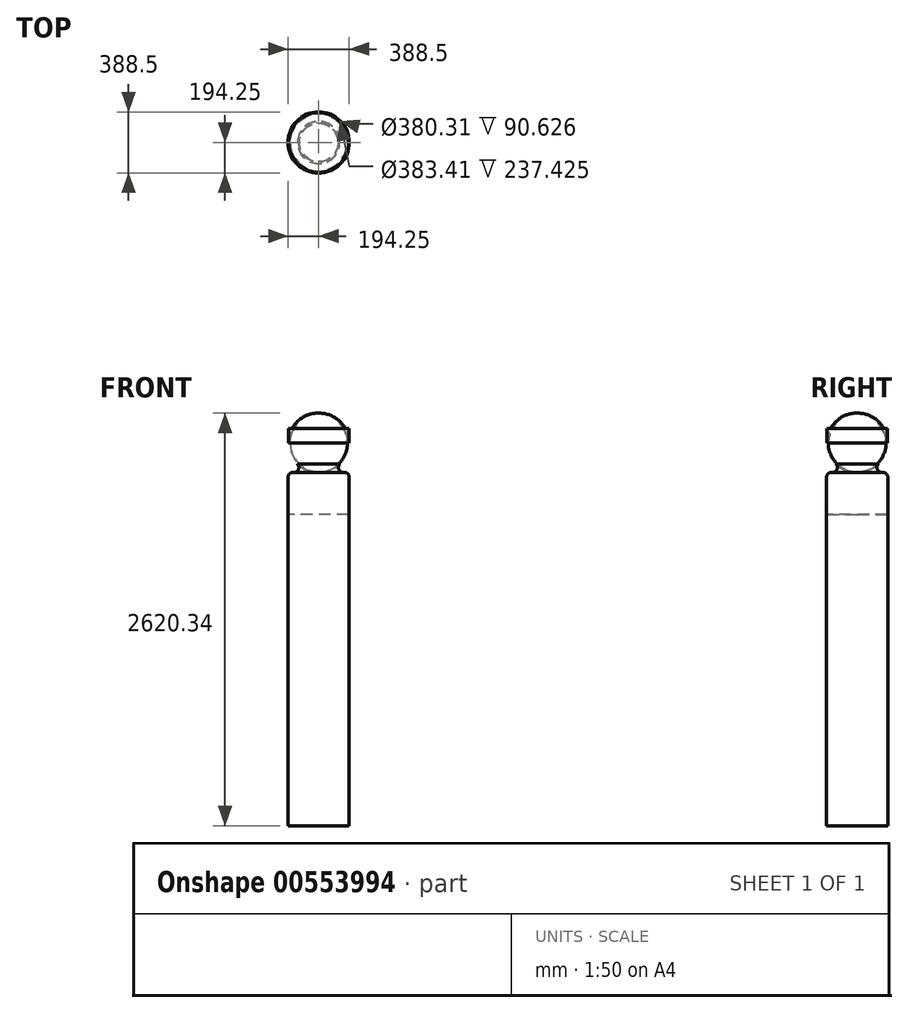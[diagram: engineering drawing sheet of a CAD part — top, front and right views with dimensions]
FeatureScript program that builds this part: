
annotation { "Feature Type Name" : "Feature", "Feature Type Description" : "" }
export const myFeature = defineFeature(function(context is Context, id is Id, definition is map)
    precondition{}
    {
        {
            var Q0;
            Q0=qCreatedBy(makeId("Top.planeOp"),FACE);
            var sketch = newSketch(context, id + "F0", { "sketchPlane" : qUnion([Q0])});
            skCircle(sketch, "E0", {"center": v(0, 0) * mm, "radius": 192.7 * mm});
            skSolve(sketch);
        }
        {
            var Q0;
            Q0=makeQuery(id+"F0.imprint","IMPRINT",FACE,{"disambiguationData":[TD([[makeQuery(id+"F0.imprint","IMPRINT",EDGE,{"derivedFrom":sQuery(id+"F0.wireOp",EDGE,"E0")}),1.0]])]});
            extrude(context, id + "F1", {"entities" : qUnion([Q0]), "depth" : 278.82 * mm, "offsetDistance" : 25.4 * mm});
        }
        {
            var Q0;
            Q0=makeQuery(id+"F1.opExtrude","CAP_FACE",FACE,{"disambiguationData":[OSD([sQuery(id+"F0.wireOp",EDGE,"E0")])],"isStart":true});
            fillet(context, id + "F2", {"entities" : qUnion([Q0]), "radius" : 188.2 * mm, "tangentPropagation" : true, "allowEdgeOverflow" : false});
        }
        {
            var Q0;
            Q0=qCreatedBy(makeId("Top.planeOp"),FACE);
            var sketch = newSketch(context, id + "F3", { "sketchPlane" : qUnion([Q0])});
            skCircle(sketch, "E1", {"center": v(0, 0) * mm, "radius": 194.25 * mm});
            skSolve(sketch);
        }
        {
            var Q0;
            Q0=makeQuery(id+"F3.imprint","IMPRINT",FACE,{"disambiguationData":[TD([[makeQuery(id+"F3.imprint","IMPRINT",EDGE,{"derivedFrom":sQuery(id+"F3.wireOp",EDGE,"E1")}),1.0]])]});
            extrude(context, id + "F4", {"entities" : qUnion([Q0]), "operationType" : NewBodyOperationType.ADD, "oppositeDirection" : true, "depth" : 270.45 * mm, "offsetDistance" : 25.4 * mm});
        }
        {
            var Q0;
            Q0=makeQuery(id+"F4.opExtrude","CAP_FACE",FACE,{"disambiguationData":[OSD([sQuery(id+"F3.wireOp",EDGE,"E1")])],"isStart":true});
            fillet(context, id + "F5", {"entities" : qUnion([Q0]), "radius" : 30.48 * mm, "tangentPropagation" : true, "allowEdgeOverflow" : false});
        }
        {
            var Q0;
            Q0=makeQuery(id+"F1.opExtrude","CAP_FACE",FACE,{"disambiguationData":[OSD([sQuery(id+"F0.wireOp",EDGE,"E0")])],"isStart":false});
            shell(context, id + "F6", {"entities" : qUnion([Q0]), "thickness" : 2.54 * mm});
        }
        {
            var Q0;
            Q0=makeQuery(id+"F4.opExtrude","CAP_FACE",FACE,{"disambiguationData":[OSD([sQuery(id+"F3.wireOp",EDGE,"E1")])],"isStart":false});
            extrude(context, id + "F7", {"entities" : qUnion([Q0]), "operationType" : NewBodyOperationType.ADD, "depth" : 843.53 * mm, "offsetDistance" : 25.4 * mm});
        }
        {
            var Q0;
            Q0=makeQuery(id+"F7.opExtrude","CAP_FACE",FACE,{"disambiguationData":[OSD([sQuery(id+"F3.wireOp",EDGE,"E1")])],"isStart":false});
            extrude(context, id + "F8", {"entities" : qUnion([Q0]), "operationType" : NewBodyOperationType.ADD, "depth" : 1129.98 * mm, "offsetDistance" : 25.4 * mm});
        }
    });
